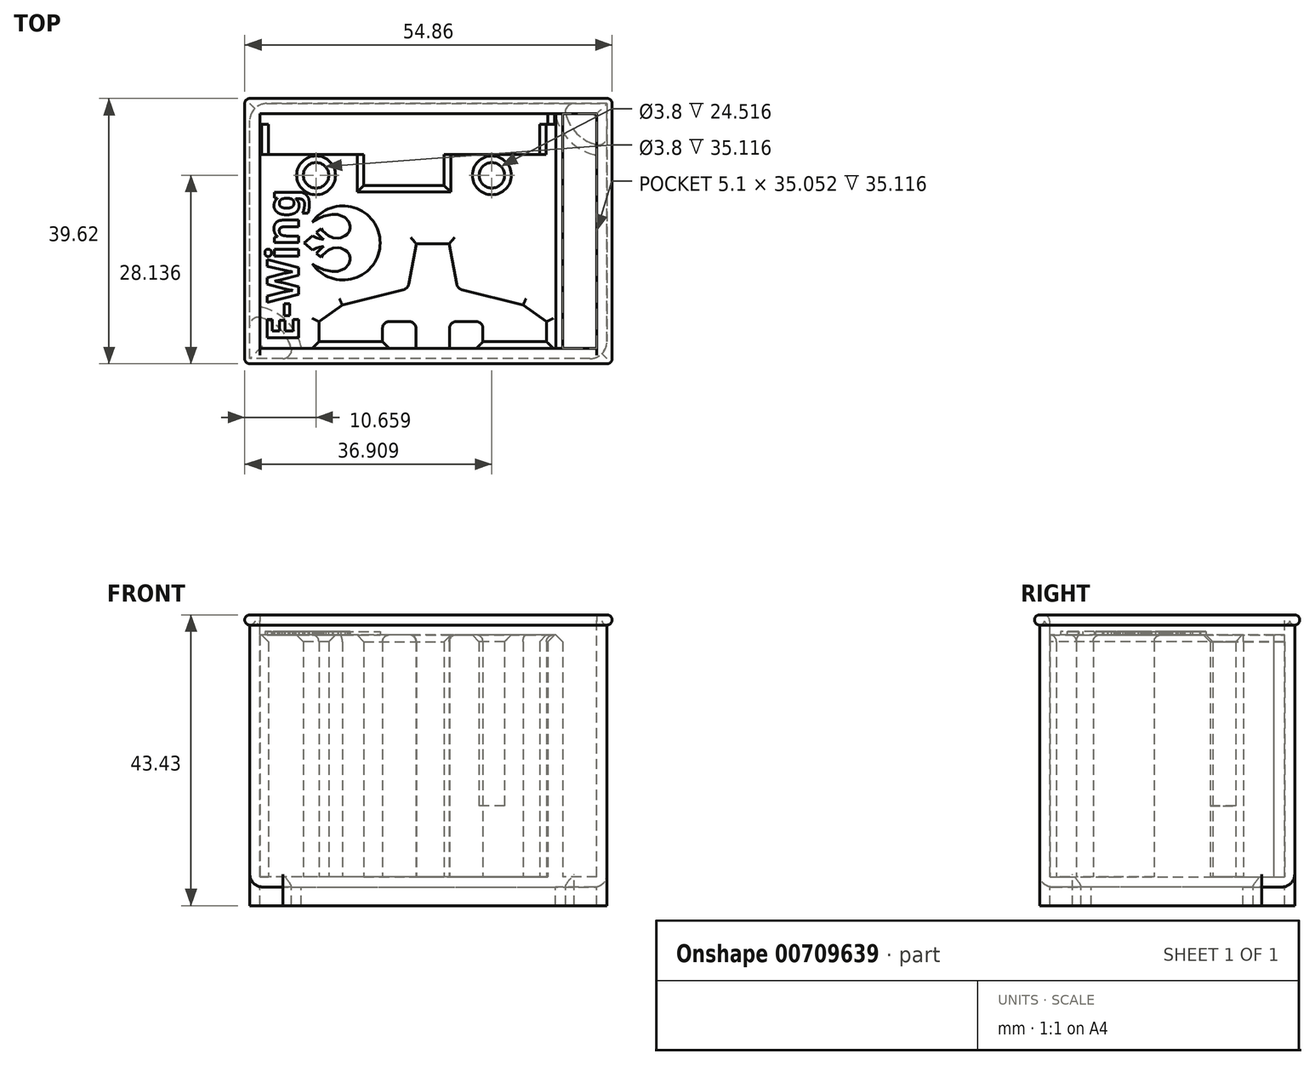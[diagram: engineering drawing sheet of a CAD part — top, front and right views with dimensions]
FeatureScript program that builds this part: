
annotation { "Feature Type Name" : "Feature", "Feature Type Description" : "" }
export const myFeature = defineFeature(function(context is Context, id is Id, definition is map)
    precondition{}
    {
        {
            var Q0;
            Q0=qCreatedBy(makeId("Front.planeOp"),FACE);
            var sketch = newSketch(context, id + "F0", { "sketchPlane" : qUnion([Q0])});
            skLineSegment(sketch, "E0.bottom", {"start": v(26.67, -20.32) * mm, "end": v(-26.67, -20.32) * mm});
            skLineSegment(sketch, "E0.top", {"start": v(26.67, 20.32) * mm, "end": v(-26.67, 20.32) * mm});
            skLineSegment(sketch, "E0.left", {"start": v(26.67, -20.32) * mm, "end": v(26.67, 20.32) * mm});
            skLineSegment(sketch, "E0.right", {"start": v(-26.67, -20.32) * mm, "end": v(-26.67, 20.32) * mm});
            skPoint(sketch, "E0.middle", {"position": v(0, 0) * mm});
            skSolve(sketch);
        }
        {
            var Q0;
            Q0=makeQuery(id+"F0.imprint","IMPRINT",FACE,{"disambiguationData":[TD([[makeQuery(id+"F0.imprint","IMPRINT",EDGE,{"derivedFrom":sQuery(id+"F0.wireOp",EDGE,"E0.bottom")}),-1.0]])]});
            extrude(context, id + "F1", {"entities" : qUnion([Q0]), "depth" : 38.1 * mm, "symmetric" : true});
        }
        {
            var Q0;
            Q0=makeQuery(id+"F1.opExtrude","SWEPT_FACE",FACE,{"disambiguationData":[OSD([sQuery(id+"F0.wireOp",EDGE,"E0.top")])]});
            shell(context, id + "F2", {"entities" : qUnion([Q0]), "thickness" : 1.52 * mm});
        }
        {
            var Q0;
            Q0=makeQuery(id+"F1.opExtrude","CAP_FACE",FACE,{"disambiguationData":[OSD([sQuery(id+"F0.wireOp",EDGE,"E0.bottom"),sQuery(id+"F0.wireOp",EDGE,"E0.top"),sQuery(id+"F0.wireOp",EDGE,"E0.left"),sQuery(id+"F0.wireOp",EDGE,"E0.right")])],"isStart":false});
            var sketch = newSketch(context, id + "F3", { "sketchPlane" : qUnion([Q0])});
            skArc(sketch, "E1", {"start": v(-26.67, 20.32) * mm, "mid": v(-27.43, 19.56) * mm, "end": v(-26.67, 18.8) * mm});
            skSolve(sketch);
        }
        {
            var Q0;
            {var subQ0=sQuery(id+"F3.wireOp",EDGE,"E1");Q0=makeQuery(id+"F3.imprint","IMPRINT",FACE,{"disambiguationData":[TD([[makeQuery(id+"F3.imprint","IMPRINT",EDGE,{"derivedFrom":subQ0}),1.0]])]});}
            var Q1;
            Q1=makeQuery(id+"F1.opExtrude","SWEPT_EDGE",EDGE,{"disambiguationData":[OSD([sQuery(id+"F0.wireOp",EDGE,"E0.top"),sQuery(id+"F0.wireOp",EDGE,"E0.right")])]});
            var Q2;
            Q2=makeQuery(id+"F1.opExtrude","CAP_EDGE",EDGE,{"disambiguationData":[OSD([sQuery(id+"F0.wireOp",EDGE,"E0.top")])],"isStart":true});
            var Q3;
            Q3=makeQuery(id+"F1.opExtrude","SWEPT_EDGE",EDGE,{"disambiguationData":[OSD([sQuery(id+"F0.wireOp",EDGE,"E0.top"),sQuery(id+"F0.wireOp",EDGE,"E0.left")])]});
            var Q4;
            Q4=makeQuery(id+"F1.opExtrude","CAP_EDGE",EDGE,{"disambiguationData":[OSD([sQuery(id+"F0.wireOp",EDGE,"E0.top")])],"isStart":false});
            sweep(context, id + "F4", {"operationType" : NewBodyOperationType.ADD, "profiles" : qUnion([Q0]), "path" : qUnion([Q1, Q2, Q3, Q4])});
        }
        {
            var Q0;
            Q0=makeQuery(id+"F1.opExtrude","SWEPT_FACE",FACE,{"disambiguationData":[OSD([sQuery(id+"F0.wireOp",EDGE,"E0.bottom")])]});
            var sketch = newSketch(context, id + "F5", { "sketchPlane" : qUnion([Q0])});
            skLineSegment(sketch, "E2.bottom", {"start": v(26.67, 19.05) * mm, "end": v(21.75, 19.05) * mm});
            skLineSegment(sketch, "E2.left", {"start": v(26.67, 19.05) * mm, "end": v(26.67, 14.13) * mm});
            skPoint(sketch, "E3.newPointA", {"position": v(20.32, 19.05) * mm});
            skArc(sketch, "E4", {"start": v(20.52, 17.46) * mm, "mid": v(22.18, 14.56) * mm, "end": v(25.08, 12.9) * mm});
            skArc(sketch, "E5.filletArc", {"start": v(21.75, 19.05) * mm, "mid": v(20.75, 18.56) * mm, "end": v(20.52, 17.46) * mm});
            skPoint(sketch, "E6.visualSharp", {"position": v(26.67, 12.7) * mm});
            skArc(sketch, "E6.filletArc", {"start": v(25.08, 12.9) * mm, "mid": v(26.18, 13.13) * mm, "end": v(26.67, 14.13) * mm});
            skArc(sketch, "E7.MirrorCS", {"start": v(-21.75, 19.05) * mm, "mid": v(-20.75, 18.56) * mm, "end": v(-20.52, 17.46) * mm});
            skArc(sketch, "E8.MirrorCS", {"start": v(-20.52, 17.46) * mm, "mid": v(-22.18, 14.56) * mm, "end": v(-25.08, 12.9) * mm});
            skArc(sketch, "E9.MirrorCS", {"start": v(-25.08, 12.9) * mm, "mid": v(-26.18, 13.13) * mm, "end": v(-26.67, 14.13) * mm});
            skLineSegment(sketch, "E10.MirrorCS", {"start": v(-26.67, 19.05) * mm, "end": v(-26.67, 14.13) * mm});
            skLineSegment(sketch, "E11.MirrorCS", {"start": v(-26.67, 19.05) * mm, "end": v(-21.75, 19.05) * mm});
            skArc(sketch, "E12.MirrorCS", {"start": v(-20.52, -17.46) * mm, "mid": v(-22.18, -14.56) * mm, "end": v(-25.08, -12.9) * mm});
            skArc(sketch, "E13.MirrorCS", {"start": v(-21.75, -19.05) * mm, "mid": v(-20.75, -18.56) * mm, "end": v(-20.52, -17.46) * mm});
            skLineSegment(sketch, "E14.MirrorCS", {"start": v(-26.67, -19.05) * mm, "end": v(-21.75, -19.05) * mm});
            skLineSegment(sketch, "E15.MirrorCS", {"start": v(-26.67, -19.05) * mm, "end": v(-26.67, -14.13) * mm});
            skArc(sketch, "E16.MirrorCS", {"start": v(-25.08, -12.9) * mm, "mid": v(-26.18, -13.13) * mm, "end": v(-26.67, -14.13) * mm});
            skArc(sketch, "E17.MirrorCS", {"start": v(21.75, -19.05) * mm, "mid": v(20.75, -18.56) * mm, "end": v(20.52, -17.46) * mm});
            skArc(sketch, "E18.MirrorCS", {"start": v(20.52, -17.46) * mm, "mid": v(22.18, -14.56) * mm, "end": v(25.08, -12.9) * mm});
            skArc(sketch, "E19.MirrorCS", {"start": v(25.08, -12.9) * mm, "mid": v(26.18, -13.13) * mm, "end": v(26.67, -14.13) * mm});
            skLineSegment(sketch, "E20.MirrorCS", {"start": v(26.67, -19.05) * mm, "end": v(26.67, -14.13) * mm});
            skLineSegment(sketch, "E21.MirrorCS", {"start": v(26.67, -19.05) * mm, "end": v(21.75, -19.05) * mm});
            skSolve(sketch);
        }
        {
            var Q0;
            Q0=makeQuery(id+"F5.imprint","IMPRINT",FACE,{"disambiguationData":[TD([[makeQuery(id+"F5.imprint","IMPRINT",EDGE,{"derivedFrom":sQuery(id+"F5.wireOp",EDGE,"E2.bottom")}),1.0]])]});
            var Q1;
            Q1=makeQuery(id+"F5.imprint","IMPRINT",FACE,{"disambiguationData":[TD([[makeQuery(id+"F5.imprint","IMPRINT",EDGE,{"derivedFrom":sQuery(id+"F5.wireOp",EDGE,"E8.MirrorCS")}),-1.0]])]});
            var Q2;
            Q2=makeQuery(id+"F5.imprint","IMPRINT",FACE,{"disambiguationData":[TD([[makeQuery(id+"F5.imprint","IMPRINT",EDGE,{"derivedFrom":sQuery(id+"F5.wireOp",EDGE,"E12.MirrorCS")}),1.0]])]});
            var Q3;
            Q3=makeQuery(id+"F5.imprint","IMPRINT",FACE,{"disambiguationData":[TD([[makeQuery(id+"F5.imprint","IMPRINT",EDGE,{"derivedFrom":sQuery(id+"F5.wireOp",EDGE,"E17.MirrorCS")}),-1.0]])]});
            extrude(context, id + "F6", {"entities" : qUnion([Q0, Q1, Q2, Q3]), "operationType" : NewBodyOperationType.ADD, "depth" : 2.8 * mm});
        }
        {
            var Q0;
            Q0=makeQuery(id+"F6.opExtrude","CAP_FACE",FACE,{"disambiguationData":[OSD([sQuery(id+"F5.wireOp",EDGE,"E2.bottom"),sQuery(id+"F5.wireOp",EDGE,"E2.left"),sQuery(id+"F5.wireOp",EDGE,"E4"),sQuery(id+"F5.wireOp",EDGE,"E5.filletArc"),sQuery(id+"F5.wireOp",EDGE,"E6.filletArc")])],"isStart":false});
            var Q1;
            Q1=makeQuery(id+"F6.opExtrude","CAP_FACE",FACE,{"disambiguationData":[OSD([sQuery(id+"F5.wireOp",EDGE,"E8.MirrorCS"),sQuery(id+"F5.wireOp",EDGE,"E9.MirrorCS"),sQuery(id+"F5.wireOp",EDGE,"E10.MirrorCS"),sQuery(id+"F5.wireOp",EDGE,"E7.MirrorCS"),sQuery(id+"F5.wireOp",EDGE,"E11.MirrorCS")])],"isStart":false});
            var Q2;
            Q2=makeQuery(id+"F6.opExtrude","CAP_FACE",FACE,{"disambiguationData":[OSD([sQuery(id+"F5.wireOp",EDGE,"E12.MirrorCS"),sQuery(id+"F5.wireOp",EDGE,"E13.MirrorCS"),sQuery(id+"F5.wireOp",EDGE,"E14.MirrorCS"),sQuery(id+"F5.wireOp",EDGE,"E15.MirrorCS"),sQuery(id+"F5.wireOp",EDGE,"E16.MirrorCS")])],"isStart":false});
            var Q3;
            Q3=makeQuery(id+"F6.opExtrude","CAP_FACE",FACE,{"disambiguationData":[OSD([sQuery(id+"F5.wireOp",EDGE,"E17.MirrorCS"),sQuery(id+"F5.wireOp",EDGE,"E18.MirrorCS"),sQuery(id+"F5.wireOp",EDGE,"E19.MirrorCS"),sQuery(id+"F5.wireOp",EDGE,"E20.MirrorCS"),sQuery(id+"F5.wireOp",EDGE,"E21.MirrorCS")])],"isStart":false});
            shell(context, id + "F7", {"entities" : qUnion([Q0, Q1, Q2, Q3]), "thickness" : 1.52 * mm});
        }
        {
            var Q0;
            Q0=makeQuery(id+"F1.opExtrude","SWEPT_EDGE",EDGE,{"disambiguationData":[OSD([sQuery(id+"F0.wireOp",EDGE,"E0.bottom"),sQuery(id+"F0.wireOp",EDGE,"E0.right")])]});
            var Q1;
            Q1=makeQuery(id+"F1.opExtrude","CAP_EDGE",EDGE,{"disambiguationData":[OSD([sQuery(id+"F0.wireOp",EDGE,"E0.bottom")])],"isStart":false});
            var Q2;
            Q2=makeQuery(id+"F1.opExtrude","SWEPT_EDGE",EDGE,{"disambiguationData":[OSD([sQuery(id+"F0.wireOp",EDGE,"E0.bottom"),sQuery(id+"F0.wireOp",EDGE,"E0.left")])]});
            var Q3;
            Q3=makeQuery(id+"F1.opExtrude","CAP_EDGE",EDGE,{"disambiguationData":[OSD([sQuery(id+"F0.wireOp",EDGE,"E0.bottom")])],"isStart":true});
            fillet(context, id + "F8", {"entities" : qUnion([Q0, Q1, Q2, Q3]), "radius" : 1.9 * mm, "tangentPropagation" : true, "allowEdgeOverflow" : false});
        }
        {
            var Q0;
            Q0=makeQuery(id+"F4.opSweep","MID_CAP_EDGE",EDGE,{"disambiguationData":[OSD([sQuery(id+"F0.wireOp",EDGE,"E0.top"),sQuery(id+"F0.wireOp",EDGE,"E0.left"),sQuery(id+"F3.wireOp",EDGE,"E1")])],"capPos":3.0});
            var Q1;
            Q1=makeQuery(id+"F4.opSweep","MID_CAP_EDGE",EDGE,{"disambiguationData":[OSD([sQuery(id+"F0.wireOp",EDGE,"E0.top"),sQuery(id+"F0.wireOp",EDGE,"E0.left"),sQuery(id+"F3.wireOp",EDGE,"E1")])],"capPos":2.0});
            var Q2;
            Q2=makeQuery(id+"F4.opSweep","MID_CAP_EDGE",EDGE,{"disambiguationData":[OSD([sQuery(id+"F0.wireOp",EDGE,"E0.top"),sQuery(id+"F0.wireOp",EDGE,"E0.right"),sQuery(id+"F3.wireOp",EDGE,"E1")])],"capPos":1.0});
            var Q3;
            Q3=makeQuery(id+"F4.opSweep","CAP_EDGE",EDGE,{"disambiguationData":[OSD([sQuery(id+"F0.wireOp",EDGE,"E0.top"),sQuery(id+"F0.wireOp",EDGE,"E0.right"),sQuery(id+"F3.wireOp",EDGE,"E1")])],"isStart":true});
            fillet(context, id + "F9", {"entities" : qUnion([Q0, Q1, Q2, Q3]), "radius" : 0.76 * mm, "tangentPropagation" : true, "allowEdgeOverflow" : false});
        }
        {
            var Q0;
            Q0=makeQuery(id+"F6.boolean.opBoolean","MERGE",EDGE,{"derivedFrom":[makeQuery(id+"F1.opExtrude","CAP_EDGE",EDGE,{"disambiguationData":[OSD([sQuery(id+"F0.wireOp",EDGE,"E0.left")])],"isStart":false}),makeQuery(id+"F6.opExtrude","SWEPT_EDGE",EDGE,{"disambiguationData":[OSD([sQuery(id+"F5.wireOp",EDGE,"E2.bottom"),sQuery(id+"F5.wireOp",EDGE,"E2.left")])]})]});
            var Q1;
            Q1=makeQuery(id+"F6.boolean.opBoolean","MERGE",EDGE,{"derivedFrom":[makeQuery(id+"F1.opExtrude","CAP_EDGE",EDGE,{"disambiguationData":[OSD([sQuery(id+"F0.wireOp",EDGE,"E0.left")])],"isStart":true}),makeQuery(id+"F6.opExtrude","SWEPT_EDGE",EDGE,{"disambiguationData":[OSD([sQuery(id+"F5.wireOp",EDGE,"E20.MirrorCS"),sQuery(id+"F5.wireOp",EDGE,"E21.MirrorCS")])]})]});
            var Q2;
            Q2=makeQuery(id+"F6.boolean.opBoolean","MERGE",EDGE,{"derivedFrom":[makeQuery(id+"F1.opExtrude","CAP_EDGE",EDGE,{"disambiguationData":[OSD([sQuery(id+"F0.wireOp",EDGE,"E0.right")])],"isStart":false}),makeQuery(id+"F6.opExtrude","SWEPT_EDGE",EDGE,{"disambiguationData":[OSD([sQuery(id+"F5.wireOp",EDGE,"E10.MirrorCS"),sQuery(id+"F5.wireOp",EDGE,"E11.MirrorCS")])]})]});
            var Q3;
            Q3=makeQuery(id+"F6.boolean.opBoolean","MERGE",EDGE,{"derivedFrom":[makeQuery(id+"F1.opExtrude","CAP_EDGE",EDGE,{"disambiguationData":[OSD([sQuery(id+"F0.wireOp",EDGE,"E0.right")])],"isStart":true}),makeQuery(id+"F6.opExtrude","SWEPT_EDGE",EDGE,{"disambiguationData":[OSD([sQuery(id+"F5.wireOp",EDGE,"E14.MirrorCS"),sQuery(id+"F5.wireOp",EDGE,"E15.MirrorCS")])]})]});
            fillet(context, id + "F10", {"entities" : qUnion([Q0, Q1, Q2, Q3]), "radius" : 2.54 * mm, "tangentPropagation" : true, "allowEdgeOverflow" : false});
        }
        {
            var Q0;
            Q0=makeQuery(id+"F2.opShell","OFFSET_FACE",FACE,{"disambiguationData":[OSD([sQuery(id+"F0.wireOp",EDGE,"E0.bottom")])]});
            var sketch = newSketch(context, id + "F11", { "sketchPlane" : qUnion([Q0])});
            skLineSegment(sketch, "E22.bottom", {"start": v(-51.93, -9.02) * mm, "end": v(-66.18, -9.02) * mm});
            skLineSegment(sketch, "E22.top", {"start": v(-51.93, -2.92) * mm, "end": v(-92.43, -2.92) * mm});
            skLineSegment(sketch, "E22.left", {"start": v(-51.93, -9.02) * mm, "end": v(-51.93, -4.52) * mm});
            skLineSegment(sketch, "E22.right", {"start": v(-92.43, -9.02) * mm, "end": v(-92.43, -4.52) * mm});
            skPoint(sketch, "E22.middle", {"position": v(-72.18, -5.97) * mm});
            skLineSegment(sketch, "E23.bottom", {"start": v(-93.68, -2.92) * mm, "end": v(-50.68, -2.92) * mm});
            skLineSegment(sketch, "E23.top", {"start": v(-93.68, -4.52) * mm, "end": v(-92.43, -4.52) * mm});
            skLineSegment(sketch, "E23.left", {"start": v(-93.68, -2.92) * mm, "end": v(-93.68, -4.52) * mm});
            skLineSegment(sketch, "E23.right", {"start": v(-50.68, -2.92) * mm, "end": v(-50.68, -4.52) * mm});
            skLineSegment(sketch, "E24.top", {"start": v(-78.18, -13.62) * mm, "end": v(-66.18, -13.62) * mm});
            skLineSegment(sketch, "E24.left", {"start": v(-78.18, -9.02) * mm, "end": v(-78.18, -13.62) * mm});
            skLineSegment(sketch, "E24.right", {"start": v(-66.18, -9.02) * mm, "end": v(-66.18, -13.62) * mm});
            skLineSegment(sketch, "E25.trimOffspring", {"start": v(-51.93, -4.52) * mm, "end": v(-50.68, -4.52) * mm});
            skLineSegment(sketch, "E26.trimOffspring", {"start": v(-78.18, -9.02) * mm, "end": v(-92.43, -9.02) * mm});
            skCircle(sketch, "E27", {"center": v(-59.06, -12.12) * mm, "radius": 1.9 * mm});
            skLineSegment(sketch, "E28", {"start": v(-59.06, -9.02) * mm, "end": v(-59.06, -10.22) * mm, "construction": true});
            skPoint(sketch, "E29.startSnap0", {"position": v(-72.18, -2.92) * mm});
            skLineSegment(sketch, "E30.MirrorCS", {"start": v(-85.3, -9.02) * mm, "end": v(-85.3, -10.22) * mm, "construction": true});
            skCircle(sketch, "E31.MirrorC", {"center": v(-85.3, -12.12) * mm, "radius": 1.9 * mm});
            skLineSegment(sketch, "E32.bottom", {"start": v(16.6, 11.43) * mm, "end": v(2.35, 11.43) * mm});
            skLineSegment(sketch, "E32.top", {"start": v(16.6, 17.53) * mm, "end": v(-23.9, 17.53) * mm});
            skLineSegment(sketch, "E32.left", {"start": v(16.6, 11.43) * mm, "end": v(16.6, 15.93) * mm});
            skLineSegment(sketch, "E32.right", {"start": v(-23.9, 11.43) * mm, "end": v(-23.9, 15.93) * mm});
            skPoint(sketch, "E32.middle", {"position": v(-3.65, 14.48) * mm});
            skLineSegment(sketch, "E33.bottom", {"start": v(-25.15, 17.53) * mm, "end": v(17.85, 17.53) * mm});
            skLineSegment(sketch, "E33.top", {"start": v(-25.15, 15.93) * mm, "end": v(-23.9, 15.93) * mm});
            skLineSegment(sketch, "E33.left", {"start": v(-25.15, 17.53) * mm, "end": v(-25.15, 15.93) * mm});
            skLineSegment(sketch, "E33.right", {"start": v(17.85, 17.53) * mm, "end": v(17.85, 15.93) * mm});
            skLineSegment(sketch, "E34.top", {"start": v(-9.65, 6.83) * mm, "end": v(2.35, 6.83) * mm});
            skLineSegment(sketch, "E34.left", {"start": v(-9.65, 11.43) * mm, "end": v(-9.65, 6.83) * mm});
            skLineSegment(sketch, "E34.right", {"start": v(2.35, 11.43) * mm, "end": v(2.35, 6.83) * mm});
            skLineSegment(sketch, "E35.trimOffspring", {"start": v(16.6, 15.93) * mm, "end": v(17.85, 15.93) * mm});
            skLineSegment(sketch, "E36.trimOffspring", {"start": v(-9.65, 11.43) * mm, "end": v(-23.9, 11.43) * mm});
            skCircle(sketch, "E37", {"center": v(9.48, 8.33) * mm, "radius": 1.9 * mm});
            skLineSegment(sketch, "E38", {"start": v(9.48, 11.43) * mm, "end": v(9.48, 10.23) * mm, "construction": true});
            skPoint(sketch, "E39.startSnap0", {"position": v(-3.65, 17.53) * mm});
            skLineSegment(sketch, "E40.MirrorCS", {"start": v(-16.77, 11.43) * mm, "end": v(-16.77, 10.23) * mm, "construction": true});
            skCircle(sketch, "E41.MirrorC", {"center": v(-16.77, 8.33) * mm, "radius": 1.9 * mm});
            skSolve(sketch);
        }
        {
            var Q0;
            Q0=makeQuery(id+"F2.opShell","OFFSET_FACE",FACE,{"disambiguationData":[OSD([sQuery(id+"F0.wireOp",EDGE,"E0.bottom")])]});
            var sketch = newSketch(context, id + "F12", { "sketchPlane" : qUnion([Q0])});
            skLineSegment(sketch, "E42.bottom", {"start": v(20.05, -17.7) * mm, "end": v(20.05, 17.7) * mm});
            skLineSegment(sketch, "E42.top", {"start": v(25.15, -17.7) * mm, "end": v(25.15, 17.7) * mm});
            skLineSegment(sketch, "E42.left", {"start": v(20.05, -17.7) * mm, "end": v(25.15, -17.7) * mm});
            skLineSegment(sketch, "E42.right", {"start": v(20.05, 17.7) * mm, "end": v(25.15, 17.7) * mm});
            skPoint(sketch, "E42.middle", {"position": v(22.6, 0) * mm});
            skSolve(sketch);
        }
        {
            var Q0;
            Q0=makeQuery(id+"F2.opShell","OFFSET_FACE",FACE,{"disambiguationData":[OSD([sQuery(id+"F0.wireOp",EDGE,"E0.bottom")])]});
            var sketch = newSketch(context, id + "F13", { "sketchPlane" : qUnion([Q0])});
            skLineSegment(sketch, "E43", {"start": v(-1.2, -17.53) * mm, "end": v(-3.65, -17.53) * mm});
            skLineSegment(sketch, "E44.MirrorCS", {"start": v(-6.1, -17.53) * mm, "end": v(-3.65, -17.53) * mm});
            skLineSegment(sketch, "E45", {"start": v(-1.15, -17.53) * mm, "end": v(-1.15, -13.53) * mm});
            skLineSegment(sketch, "E46", {"start": v(-1.15, -13.53) * mm, "end": v(3.85, -13.53) * mm});
            skLineSegment(sketch, "E47", {"start": v(3.85, -13.53) * mm, "end": v(3.85, -16.53) * mm});
            skPoint(sketch, "E48.visualSharp", {"position": v(3.85, -13.53) * mm});
            skPoint(sketch, "E49.visualSharp", {"position": v(-1.15, -13.53) * mm});
            skLineSegment(sketch, "E50", {"start": v(-1.15, -17.53) * mm, "end": v(-3.65, -17.53) * mm});
            skLineSegment(sketch, "E51", {"start": v(-1.2, -1.93) * mm, "end": v(-3.65, -1.93) * mm});
            skLineSegment(sketch, "E52", {"start": v(13.35, -16.53) * mm, "end": v(13.35, -13.53) * mm});
            skLineSegment(sketch, "E53", {"start": v(0.05, -8.58) * mm, "end": v(9.85, -11.03) * mm});
            skLineSegment(sketch, "E54", {"start": v(9.85, -11.03) * mm, "end": v(13.35, -13.53) * mm});
            skLineSegment(sketch, "E55", {"start": v(3.85, -16.53) * mm, "end": v(13.35, -16.53) * mm});
            skLineSegment(sketch, "E56", {"start": v(-1.2, -1.93) * mm, "end": v(0.05, -8.58) * mm});
            skLineSegment(sketch, "E57.MirrorCS", {"start": v(-6.1, -1.93) * mm, "end": v(-3.65, -1.93) * mm});
            skLineSegment(sketch, "E58.MirrorCS", {"start": v(-11.15, -13.53) * mm, "end": v(-11.15, -16.53) * mm});
            skLineSegment(sketch, "E59.MirrorCS", {"start": v(-6.15, -13.53) * mm, "end": v(-11.15, -13.53) * mm});
            skLineSegment(sketch, "E60.MirrorCS", {"start": v(-6.15, -17.53) * mm, "end": v(-3.65, -17.53) * mm});
            skLineSegment(sketch, "E61.MirrorCS", {"start": v(-11.15, -16.53) * mm, "end": v(-20.65, -16.53) * mm});
            skLineSegment(sketch, "E62.MirrorCS", {"start": v(-6.15, -17.53) * mm, "end": v(-6.15, -13.53) * mm});
            skPoint(sketch, "E63.MirrorP", {"position": v(-6.15, -13.53) * mm});
            skPoint(sketch, "E64.MirrorP", {"position": v(-11.15, -13.53) * mm});
            skLineSegment(sketch, "E65.MirrorCS", {"start": v(-20.65, -16.53) * mm, "end": v(-20.65, -13.53) * mm});
            skLineSegment(sketch, "E66.MirrorCS", {"start": v(-7.34, -8.58) * mm, "end": v(-17.15, -11.03) * mm});
            skLineSegment(sketch, "E67.MirrorCS", {"start": v(-6.1, -1.93) * mm, "end": v(-7.34, -8.58) * mm});
            skLineSegment(sketch, "E68.MirrorCS", {"start": v(-17.15, -11.03) * mm, "end": v(-20.65, -13.53) * mm});
            skPoint(sketch, "E69.0", {"position": v(-3.65, 6.83) * mm});
            skSolve(sketch);
        }
        {
            var Q0;
            Q0=makeQuery(id+"F2.opShell","OFFSET_FACE",FACE,{"disambiguationData":[OSD([sQuery(id+"F0.wireOp",EDGE,"E0.bottom")])]});
            var sketch = newSketch(context, id + "F14", { "sketchPlane" : qUnion([Q0])});
            skLineSegment(sketch, "E70.0", {"start": v(3.1, -17.53) * mm, "end": v(0.65, -17.53) * mm});
            skLineSegment(sketch, "E70.1", {"start": v(-1.8, -17.53) * mm, "end": v(0.65, -17.53) * mm});
            skLineSegment(sketch, "E70.2", {"start": v(3.15, -17.53) * mm, "end": v(3.15, -13.53) * mm});
            skLineSegment(sketch, "E70.3", {"start": v(3.15, -13.53) * mm, "end": v(8.15, -13.53) * mm});
            skLineSegment(sketch, "E70.4", {"start": v(8.15, -13.53) * mm, "end": v(8.15, -16.53) * mm});
            skPoint(sketch, "E70.5", {"position": v(8.15, -13.53) * mm});
            skPoint(sketch, "E70.6", {"position": v(3.15, -13.53) * mm});
            skLineSegment(sketch, "E70.7", {"start": v(3.15, -17.53) * mm, "end": v(0.65, -17.53) * mm});
            skLineSegment(sketch, "E70.8", {"start": v(3.1, -1.93) * mm, "end": v(0.65, -1.93) * mm});
            skLineSegment(sketch, "E70.9", {"start": v(17.65, -16.53) * mm, "end": v(17.65, -13.53) * mm});
            skLineSegment(sketch, "E70.10", {"start": v(4.34, -8.58) * mm, "end": v(14.15, -11.03) * mm});
            skLineSegment(sketch, "E70.11", {"start": v(14.15, -11.03) * mm, "end": v(17.65, -13.53) * mm});
            skLineSegment(sketch, "E70.12", {"start": v(8.15, -16.53) * mm, "end": v(17.65, -16.53) * mm});
            skLineSegment(sketch, "E70.13", {"start": v(3.1, -1.93) * mm, "end": v(4.34, -8.58) * mm});
            skLineSegment(sketch, "E70.14", {"start": v(-1.8, -1.93) * mm, "end": v(0.65, -1.93) * mm});
            skLineSegment(sketch, "E70.15", {"start": v(-6.85, -13.53) * mm, "end": v(-6.85, -16.53) * mm});
            skLineSegment(sketch, "E70.16", {"start": v(-1.85, -13.53) * mm, "end": v(-6.85, -13.53) * mm});
            skLineSegment(sketch, "E70.17", {"start": v(-1.85, -17.53) * mm, "end": v(0.65, -17.53) * mm});
            skLineSegment(sketch, "E70.18", {"start": v(-6.85, -16.53) * mm, "end": v(-16.35, -16.53) * mm});
            skLineSegment(sketch, "E70.19", {"start": v(-1.85, -17.53) * mm, "end": v(-1.85, -13.53) * mm});
            skPoint(sketch, "E70.20", {"position": v(-1.85, -13.53) * mm});
            skPoint(sketch, "E70.21", {"position": v(-6.85, -13.53) * mm});
            skLineSegment(sketch, "E70.22", {"start": v(-16.35, -16.53) * mm, "end": v(-16.35, -13.53) * mm});
            skLineSegment(sketch, "E70.23", {"start": v(-3.05, -8.58) * mm, "end": v(-12.85, -11.03) * mm});
            skLineSegment(sketch, "E70.24", {"start": v(-1.8, -1.93) * mm, "end": v(-3.05, -8.58) * mm});
            skLineSegment(sketch, "E70.25", {"start": v(-12.85, -11.03) * mm, "end": v(-16.35, -13.53) * mm});
            skPoint(sketch, "E70.26", {"position": v(-3.65, 6.83) * mm});
            skLineSegment(sketch, "E71.0", {"start": v(20.05, -17.7) * mm, "end": v(20.05, 17.7) * mm});
            skLineSegment(sketch, "E71.1", {"start": v(25.15, -17.7) * mm, "end": v(25.15, 17.7) * mm});
            skLineSegment(sketch, "E71.2", {"start": v(20.05, -17.7) * mm, "end": v(25.15, -17.7) * mm});
            skLineSegment(sketch, "E71.3", {"start": v(20.05, 17.7) * mm, "end": v(25.15, 17.7) * mm});
            skPoint(sketch, "E71.4", {"position": v(22.6, 0) * mm});
            skLineSegment(sketch, "E71.5", {"start": v(-51.93, -9.02) * mm, "end": v(-66.18, -9.02) * mm});
            skLineSegment(sketch, "E71.6", {"start": v(-51.93, -2.92) * mm, "end": v(-92.43, -2.92) * mm});
            skLineSegment(sketch, "E71.7", {"start": v(-51.93, -9.02) * mm, "end": v(-51.93, -4.52) * mm});
            skLineSegment(sketch, "E71.8", {"start": v(-92.43, -9.02) * mm, "end": v(-92.43, -4.52) * mm});
            skPoint(sketch, "E71.9", {"position": v(-72.18, -5.97) * mm});
            skLineSegment(sketch, "E71.10", {"start": v(-93.68, -2.92) * mm, "end": v(-50.68, -2.92) * mm});
            skLineSegment(sketch, "E71.11", {"start": v(-93.68, -4.52) * mm, "end": v(-92.43, -4.52) * mm});
            skLineSegment(sketch, "E71.12", {"start": v(-93.68, -2.92) * mm, "end": v(-93.68, -4.52) * mm});
            skLineSegment(sketch, "E71.13", {"start": v(-50.68, -2.92) * mm, "end": v(-50.68, -4.52) * mm});
            skLineSegment(sketch, "E71.14", {"start": v(-78.18, -13.62) * mm, "end": v(-66.18, -13.62) * mm});
            skLineSegment(sketch, "E71.15", {"start": v(-78.18, -9.02) * mm, "end": v(-78.18, -13.62) * mm});
            skLineSegment(sketch, "E71.16", {"start": v(-66.18, -9.02) * mm, "end": v(-66.18, -13.62) * mm});
            skLineSegment(sketch, "E71.17", {"start": v(-51.93, -4.52) * mm, "end": v(-50.68, -4.52) * mm});
            skLineSegment(sketch, "E71.18", {"start": v(-78.18, -9.02) * mm, "end": v(-92.43, -9.02) * mm});
            skCircle(sketch, "E71.19", {"center": v(-59.06, -12.12) * mm, "radius": 1.9 * mm});
            skLineSegment(sketch, "E71.20", {"start": v(-59.06, -9.02) * mm, "end": v(-59.06, -10.22) * mm});
            skPoint(sketch, "E71.21", {"position": v(-72.18, -2.92) * mm});
            skLineSegment(sketch, "E71.22", {"start": v(-85.3, -9.02) * mm, "end": v(-85.3, -10.22) * mm});
            skCircle(sketch, "E71.23", {"center": v(-85.3, -12.12) * mm, "radius": 1.9 * mm});
            skLineSegment(sketch, "E71.24", {"start": v(16.6, 11.43) * mm, "end": v(2.35, 11.43) * mm});
            skLineSegment(sketch, "E71.25", {"start": v(16.6, 17.53) * mm, "end": v(-23.9, 17.53) * mm});
            skLineSegment(sketch, "E71.26", {"start": v(16.6, 11.43) * mm, "end": v(16.6, 15.93) * mm});
            skLineSegment(sketch, "E71.27", {"start": v(-23.9, 11.43) * mm, "end": v(-23.9, 15.93) * mm});
            skPoint(sketch, "E71.28", {"position": v(-3.65, 14.48) * mm});
            skLineSegment(sketch, "E71.29", {"start": v(-25.15, 17.53) * mm, "end": v(17.85, 17.53) * mm});
            skLineSegment(sketch, "E71.30", {"start": v(-25.15, 15.93) * mm, "end": v(-23.9, 15.93) * mm});
            skLineSegment(sketch, "E71.31", {"start": v(-25.15, 17.53) * mm, "end": v(-25.15, 15.93) * mm});
            skLineSegment(sketch, "E71.32", {"start": v(17.85, 17.53) * mm, "end": v(17.85, 15.93) * mm});
            skLineSegment(sketch, "E71.33", {"start": v(-9.65, 6.83) * mm, "end": v(2.35, 6.83) * mm});
            skLineSegment(sketch, "E71.34", {"start": v(-9.65, 11.43) * mm, "end": v(-9.65, 6.83) * mm});
            skLineSegment(sketch, "E71.35", {"start": v(2.35, 11.43) * mm, "end": v(2.35, 6.83) * mm});
            skLineSegment(sketch, "E71.36", {"start": v(16.6, 15.93) * mm, "end": v(17.85, 15.93) * mm});
            skLineSegment(sketch, "E71.37", {"start": v(-9.65, 11.43) * mm, "end": v(-23.9, 11.43) * mm});
            skCircle(sketch, "E71.38", {"center": v(9.48, 8.33) * mm, "radius": 1.9 * mm});
            skLineSegment(sketch, "E71.39", {"start": v(9.48, 11.43) * mm, "end": v(9.48, 10.23) * mm});
            skPoint(sketch, "E71.40", {"position": v(-3.65, 17.53) * mm});
            skLineSegment(sketch, "E71.41", {"start": v(-16.77, 11.43) * mm, "end": v(-16.77, 10.23) * mm});
            skCircle(sketch, "E71.42", {"center": v(-16.77, 8.33) * mm, "radius": 1.9 * mm});
            skLineSegment(sketch, "E72", {"start": v(17.65, -16.53) * mm, "end": v(20.05, -16.53) * mm, "construction": true});
            skSolve(sketch);
        }
        {
            var Q0;
            Q0=makeQuery(id+"F14.imprint","IMPRINT",FACE,{"disambiguationData":[TD([[makeQuery(id+"F14.imprint","IMPRINT",EDGE,{"derivedFrom":sQuery(id+"F14.wireOp",EDGE,"E71.42")}),-1.0]])]});
            var Q1;
            Q1=makeQuery(id+"F14.imprint","IMPRINT",FACE,{"disambiguationData":[TD([[makeQuery(id+"F14.imprint","IMPRINT",EDGE,{"derivedFrom":sQuery(id+"F14.wireOp",EDGE,"E71.38")}),1.0]])]});
            extrude(context, id + "F15", {"entities" : qUnion([Q0, Q1]), "operationType" : NewBodyOperationType.ADD, "depth" : 10.6 * mm, "offsetDistance" : 25 * mm});
        }
        {
            var Q0;
            {var subQ19=sQuery(id+"F14.wireOp",EDGE,"E70.2");Q0=makeQuery(id+"F14.imprint","IMPRINT",FACE,{"disambiguationData":[TD([[makeQuery(id+"F14.imprint","IMPRINT",EDGE,{"derivedFrom":subQ19}),-1.0]])]});}
            extrude(context, id + "F16", {"entities" : qUnion([Q0]), "operationType" : NewBodyOperationType.ADD, "depth" : 36.12 * mm, "offsetDistance" : 25 * mm});
        }
        {
            var Q0;
            Q0=makeQuery(id+"F16.opExtrude","CAP_EDGE",EDGE,{"disambiguationData":[OSD([sQuery(id+"F14.wireOp",EDGE,"E71.38")])],"isStart":false});
            var Q1;
            Q1=makeQuery(id+"F16.opExtrude","CAP_EDGE",EDGE,{"disambiguationData":[OSD([sQuery(id+"F14.wireOp",EDGE,"E71.42")])],"isStart":false});
            chamfer(context, id + "F17", {"entities" : qUnion([Q0, Q1]), "width" : 1 * mm, "tangentPropagation" : true});
        }
        {
            var Q0;
            Q0=makeQuery(id+"F16.opExtrude","CAP_EDGE",EDGE,{"disambiguationData":[OSD([sQuery(id+"F14.wireOp",EDGE,"E71.34")])],"isStart":false});
            var Q1;
            Q1=makeQuery(id+"F16.opExtrude","CAP_EDGE",EDGE,{"disambiguationData":[OSD([sQuery(id+"F14.wireOp",EDGE,"E71.33")])],"isStart":false});
            var Q2;
            Q2=makeQuery(id+"F16.opExtrude","CAP_EDGE",EDGE,{"disambiguationData":[OSD([sQuery(id+"F14.wireOp",EDGE,"E71.35")])],"isStart":false});
            var Q3;
            Q3=makeQuery(id+"F16.opExtrude","CAP_EDGE",EDGE,{"disambiguationData":[OSD([sQuery(id+"F14.wireOp",EDGE,"E71.26")])],"isStart":false});
            var Q4;
            Q4=makeQuery(id+"F16.opExtrude","CAP_EDGE",EDGE,{"disambiguationData":[OSD([sQuery(id+"F14.wireOp",EDGE,"E71.27")])],"isStart":false});
            var Q5;
            Q5=makeQuery(id+"F16.opExtrude","CAP_EDGE",EDGE,{"disambiguationData":[OSD([sQuery(id+"F14.wireOp",EDGE,"E71.32")])],"isStart":false});
            var Q6;
            Q6=makeQuery(id+"F16.opExtrude","CAP_EDGE",EDGE,{"disambiguationData":[OSD([sQuery(id+"F14.wireOp",EDGE,"E71.0")])],"isStart":false});
            chamfer(context, id + "F18", {"entities" : qUnion([Q0, Q1, Q2, Q3, Q4, Q5, Q6]), "width" : 1 * mm, "tangentPropagation" : true});
        }
        {
            var Q0;
            Q0=makeQuery(id+"F16.opExtrude","CAP_EDGE",EDGE,{"disambiguationData":[OSD([sQuery(id+"F14.wireOp",EDGE,"E70.24")])],"isStart":false});
            var Q1;
            Q1=makeQuery(id+"F16.opExtrude","CAP_EDGE",EDGE,{"disambiguationData":[OSD([sQuery(id+"F14.wireOp",EDGE,"E70.8"),sQuery(id+"F14.wireOp",EDGE,"E70.14")])],"isStart":false});
            var Q2;
            Q2=makeQuery(id+"F16.opExtrude","CAP_EDGE",EDGE,{"disambiguationData":[OSD([sQuery(id+"F14.wireOp",EDGE,"E70.13")])],"isStart":false});
            var Q3;
            Q3=makeQuery(id+"F16.opExtrude","CAP_EDGE",EDGE,{"disambiguationData":[OSD([sQuery(id+"F14.wireOp",EDGE,"E70.11")])],"isStart":false});
            var Q4;
            Q4=makeQuery(id+"F16.opExtrude","CAP_EDGE",EDGE,{"disambiguationData":[OSD([sQuery(id+"F14.wireOp",EDGE,"E70.10")])],"isStart":false});
            var Q5;
            Q5=makeQuery(id+"F16.opExtrude","CAP_EDGE",EDGE,{"disambiguationData":[OSD([sQuery(id+"F14.wireOp",EDGE,"E70.9")])],"isStart":false});
            var Q6;
            Q6=makeQuery(id+"F16.opExtrude","CAP_EDGE",EDGE,{"disambiguationData":[OSD([sQuery(id+"F14.wireOp",EDGE,"E70.12")])],"isStart":false});
            var Q7;
            Q7=makeQuery(id+"F16.opExtrude","CAP_EDGE",EDGE,{"disambiguationData":[OSD([sQuery(id+"F14.wireOp",EDGE,"E70.3")])],"isStart":false});
            var Q8;
            {var subQ1=sQuery(id+"F14.wireOp",EDGE,"E70.2");var subQ5=sQuery(id+"F0.wireOp",EDGE,"E0.top");Q8=makeQuery(id+"F16.boolean.opBoolean","SPLIT",EDGE,{"disambiguationData":[TD([makeQuery(id+"F16.opExtrude","SWEPT_FACE",FACE,{"disambiguationData":[OSD([subQ1])]})])],"derivedFrom":makeQuery(id+"F2.opShell","OFFSET_EDGE",EDGE,{"disambiguationData":[OSD([subQ5]),TDD([makeQuery(id+"F1.opExtrude","CAP_EDGE",EDGE,{"disambiguationData":[OSD([subQ5])],"isStart":false})])]})});}
            var Q9;
            Q9=makeQuery(id+"F16.opExtrude","CAP_EDGE",EDGE,{"disambiguationData":[OSD([sQuery(id+"F14.wireOp",EDGE,"E70.16")])],"isStart":false});
            var Q10;
            Q10=makeQuery(id+"F16.opExtrude","CAP_EDGE",EDGE,{"disambiguationData":[OSD([sQuery(id+"F14.wireOp",EDGE,"E70.18")])],"isStart":false});
            var Q11;
            Q11=makeQuery(id+"F16.opExtrude","CAP_EDGE",EDGE,{"disambiguationData":[OSD([sQuery(id+"F14.wireOp",EDGE,"E70.2")])],"isStart":false});
            var Q12;
            Q12=makeQuery(id+"F16.opExtrude","CAP_EDGE",EDGE,{"disambiguationData":[OSD([sQuery(id+"F14.wireOp",EDGE,"E70.19")])],"isStart":false});
            var Q13;
            Q13=makeQuery(id+"F16.opExtrude","CAP_EDGE",EDGE,{"disambiguationData":[OSD([sQuery(id+"F14.wireOp",EDGE,"E70.4")])],"isStart":false});
            var Q14;
            Q14=makeQuery(id+"F16.opExtrude","CAP_EDGE",EDGE,{"disambiguationData":[OSD([sQuery(id+"F14.wireOp",EDGE,"E70.15")])],"isStart":false});
            var Q15;
            Q15=makeQuery(id+"F16.opExtrude","CAP_EDGE",EDGE,{"disambiguationData":[OSD([sQuery(id+"F14.wireOp",EDGE,"E70.23")])],"isStart":false});
            var Q16;
            Q16=makeQuery(id+"F16.opExtrude","CAP_EDGE",EDGE,{"disambiguationData":[OSD([sQuery(id+"F14.wireOp",EDGE,"E70.22")])],"isStart":false});
            var Q17;
            Q17=makeQuery(id+"F16.opExtrude","CAP_EDGE",EDGE,{"disambiguationData":[OSD([sQuery(id+"F14.wireOp",EDGE,"E70.25")])],"isStart":false});
            var Q18;
            Q18=makeQuery(id+"F16.opExtrude","SWEPT_EDGE",EDGE,{"disambiguationData":[OSD([sQuery(id+"F14.wireOp",EDGE,"E70.15"),sQuery(id+"F14.wireOp",EDGE,"E70.16")])]});
            var Q19;
            Q19=makeQuery(id+"F16.opExtrude","SWEPT_EDGE",EDGE,{"disambiguationData":[OSD([sQuery(id+"F14.wireOp",EDGE,"E70.16"),sQuery(id+"F14.wireOp",EDGE,"E70.19")])]});
            var Q20;
            Q20=makeQuery(id+"F16.opExtrude","SWEPT_EDGE",EDGE,{"disambiguationData":[OSD([sQuery(id+"F14.wireOp",EDGE,"E70.2"),sQuery(id+"F14.wireOp",EDGE,"E70.3")])]});
            var Q21;
            Q21=makeQuery(id+"F16.opExtrude","SWEPT_EDGE",EDGE,{"disambiguationData":[OSD([sQuery(id+"F14.wireOp",EDGE,"E70.3"),sQuery(id+"F14.wireOp",EDGE,"E70.4")])]});
            var Q22;
            Q22=makeQuery(id+"F16.opExtrude","SWEPT_EDGE",EDGE,{"disambiguationData":[OSD([sQuery(id+"F14.wireOp",EDGE,"E70.10"),sQuery(id+"F14.wireOp",EDGE,"E70.13")])]});
            var Q23;
            Q23=makeQuery(id+"F16.opExtrude","SWEPT_EDGE",EDGE,{"disambiguationData":[OSD([sQuery(id+"F14.wireOp",EDGE,"E70.23"),sQuery(id+"F14.wireOp",EDGE,"E70.24")])]});
            fillet(context, id + "F19", {"entities" : qUnion([Q0, Q1, Q2, Q3, Q4, Q5, Q6, Q7, Q8, Q9, Q10, Q11, Q12, Q13, Q14, Q15, Q16, Q17, Q18, Q19, Q20, Q21, Q22, Q23]), "radius" : 1 * mm, "tangentPropagation" : true, "allowEdgeOverflow" : false});
        }
        {
            var Q0;
            Q0=makeQuery(id+"F19.opFillet","SPLIT",FACE,{"disambiguationData":[OD(1.0)],"derivedFrom":makeQuery(id+"F16.opExtrude","CAP_FACE",FACE,{"disambiguationData":[OSD([sQuery(id+"F0.wireOp",EDGE,"E0.bottom"),sQuery(id+"F0.wireOp",EDGE,"E0.right"),sQuery(id+"F14.wireOp",EDGE,"E70.2"),sQuery(id+"F14.wireOp",EDGE,"E70.3"),sQuery(id+"F14.wireOp",EDGE,"E70.4"),sQuery(id+"F14.wireOp",EDGE,"E70.8"),sQuery(id+"F14.wireOp",EDGE,"E70.9"),sQuery(id+"F14.wireOp",EDGE,"E70.10"),sQuery(id+"F14.wireOp",EDGE,"E70.11"),sQuery(id+"F14.wireOp",EDGE,"E70.12"),sQuery(id+"F14.wireOp",EDGE,"E70.13"),sQuery(id+"F14.wireOp",EDGE,"E70.14"),sQuery(id+"F14.wireOp",EDGE,"E70.15"),sQuery(id+"F14.wireOp",EDGE,"E70.16"),sQuery(id+"F14.wireOp",EDGE,"E70.18"),sQuery(id+"F14.wireOp",EDGE,"E70.19"),sQuery(id+"F14.wireOp",EDGE,"E70.22"),sQuery(id+"F14.wireOp",EDGE,"E70.23"),sQuery(id+"F14.wireOp",EDGE,"E70.24"),sQuery(id+"F14.wireOp",EDGE,"E70.25"),sQuery(id+"F14.wireOp",EDGE,"E71.0"),sQuery(id+"F14.wireOp",EDGE,"E71.24"),sQuery(id+"F14.wireOp",EDGE,"E71.26"),sQuery(id+"F14.wireOp",EDGE,"E71.27"),sQuery(id+"F14.wireOp",EDGE,"E71.30"),sQuery(id+"F14.wireOp",EDGE,"E71.32"),sQuery(id+"F14.wireOp",EDGE,"E71.33"),sQuery(id+"F14.wireOp",EDGE,"E71.34"),sQuery(id+"F14.wireOp",EDGE,"E71.35"),sQuery(id+"F14.wireOp",EDGE,"E71.36"),sQuery(id+"F14.wireOp",EDGE,"E71.37"),sQuery(id+"F14.wireOp",EDGE,"E71.38"),sQuery(id+"F14.wireOp",EDGE,"E71.42")])],"isStart":false})});
            var sketch = newSketch(context, id + "F20", { "sketchPlane" : qUnion([Q0])});
            skLineSegment(sketch, "E73", {"start": v(-7.29, -37.09) * mm, "end": v(-7.29, -38.29) * mm, "construction": true});
            skLineSegment(sketch, "E74", {"start": v(-68.25, -18.83) * mm, "end": v(-68.25, -49.19) * mm, "construction": true});
            skCircle(sketch, "E75", {"center": v(-12.73, -1.77) * mm, "radius": 6.35 * mm});
            skLineSegment(sketch, "E76", {"start": v(-17.3, -0.68) * mm, "end": v(-18.54, -1.77) * mm});
            skLineSegment(sketch, "E77", {"start": v(-16.74, -0.18) * mm, "end": v(-16.03, 0.37) * mm});
            skLineSegment(sketch, "E78", {"start": v(-16.03, 0.37) * mm, "end": v(-15.8, 0.07) * mm});
            skLineSegment(sketch, "E79", {"start": v(-15.8, 0.07) * mm, "end": v(-15.34, -0.38) * mm});
            skLineSegment(sketch, "E80", {"start": v(-15.34, -0.38) * mm, "end": v(-14.94, -0.7) * mm});
            skLineSegment(sketch, "E81", {"start": v(-14.94, -0.7) * mm, "end": v(-14.24, -1) * mm});
            skLineSegment(sketch, "E82", {"start": v(-14.24, -1) * mm, "end": v(-13.49, -1.08) * mm});
            skLineSegment(sketch, "E83", {"start": v(-13.49, -1.08) * mm, "end": v(-13.12, -1) * mm});
            skLineSegment(sketch, "E84", {"start": v(-13.12, -1) * mm, "end": v(-12.43, -0.7) * mm});
            skLineSegment(sketch, "E85", {"start": v(-12.43, -0.7) * mm, "end": v(-12.11, -0.5) * mm});
            skLineSegment(sketch, "E86", {"start": v(-12.11, -0.5) * mm, "end": v(-11.82, -0.07) * mm});
            skLineSegment(sketch, "E87", {"start": v(-11.82, -0.07) * mm, "end": v(-11.67, 0.42) * mm});
            skLineSegment(sketch, "E88", {"start": v(-11.67, 0.42) * mm, "end": v(-11.67, 0.8) * mm});
            skLineSegment(sketch, "E89", {"start": v(-11.67, 0.8) * mm, "end": v(-11.86, 1.4) * mm});
            skLineSegment(sketch, "E90", {"start": v(-11.86, 1.4) * mm, "end": v(-12.48, 2.05) * mm});
            skLineSegment(sketch, "E91", {"start": v(-12.48, 2.05) * mm, "end": v(-13.51, 2.5) * mm});
            skLineSegment(sketch, "E92", {"start": v(-13.51, 2.5) * mm, "end": v(-14.4, 2.5) * mm});
            skLineSegment(sketch, "E93", {"start": v(-14.4, 2.5) * mm, "end": v(-15.64, 2.22) * mm});
            skLineSegment(sketch, "E94", {"start": v(-15.64, 2.22) * mm, "end": v(-16.35, 1.92) * mm});
            skLineSegment(sketch, "E95", {"start": v(-16.35, 1.92) * mm, "end": v(-16.9, 1.63) * mm});
            skLineSegment(sketch, "E96", {"start": v(-16.9, 1.63) * mm, "end": v(-17.31, 1.33) * mm});
            skLineSegment(sketch, "E97", {"start": v(-16.74, -0.18) * mm, "end": v(-16.58, -0.39) * mm});
            skLineSegment(sketch, "E98", {"start": v(-16.58, -0.39) * mm, "end": v(-16.22, -0.75) * mm});
            skLineSegment(sketch, "E99", {"start": v(-16.22, -0.75) * mm, "end": v(-15.95, -1.03) * mm});
            skLineSegment(sketch, "E100", {"start": v(-15.95, -1.03) * mm, "end": v(-15.64, -1.24) * mm});
            skLineSegment(sketch, "E101", {"start": v(-15.64, -1.24) * mm, "end": v(-16.27, -1.15) * mm});
            skLineSegment(sketch, "E102", {"start": v(-16.27, -1.15) * mm, "end": v(-16.74, -0.99) * mm});
            skLineSegment(sketch, "E103", {"start": v(-16.74, -0.99) * mm, "end": v(-17.08, -0.85) * mm});
            skLineSegment(sketch, "E104", {"start": v(-17.08, -0.85) * mm, "end": v(-17.3, -0.68) * mm});
            skPoint(sketch, "E105.start.orphan", {"position": v(-19.08, -1.77) * mm});
            skLineSegment(sketch, "E106.MirrorCS", {"start": v(-12.11, -3.04) * mm, "end": v(-11.82, -3.47) * mm});
            skLineSegment(sketch, "E107.MirrorCS", {"start": v(-16.35, -5.46) * mm, "end": v(-16.9, -5.17) * mm});
            skLineSegment(sketch, "E108.MirrorCS", {"start": v(-12.43, -2.84) * mm, "end": v(-12.11, -3.04) * mm});
            skLineSegment(sketch, "E109.MirrorCS", {"start": v(-13.51, -6.05) * mm, "end": v(-14.4, -6.05) * mm});
            skLineSegment(sketch, "E110.MirrorCS", {"start": v(-15.64, -2.3) * mm, "end": v(-16.27, -2.4) * mm});
            skLineSegment(sketch, "E111.MirrorCS", {"start": v(-15.8, -3.61) * mm, "end": v(-15.34, -3.16) * mm});
            skLineSegment(sketch, "E112.MirrorCS", {"start": v(-16.27, -2.4) * mm, "end": v(-16.74, -2.55) * mm});
            skLineSegment(sketch, "E113.MirrorCS", {"start": v(-16.74, -2.55) * mm, "end": v(-17.08, -2.7) * mm});
            skLineSegment(sketch, "E114.MirrorCS", {"start": v(-15.95, -2.51) * mm, "end": v(-15.64, -2.3) * mm});
            skLineSegment(sketch, "E115.MirrorCS", {"start": v(-11.67, -4.34) * mm, "end": v(-11.86, -4.95) * mm});
            skLineSegment(sketch, "E116.MirrorCS", {"start": v(-11.86, -4.95) * mm, "end": v(-12.48, -5.6) * mm});
            skLineSegment(sketch, "E117.MirrorCS", {"start": v(-16.9, -5.17) * mm, "end": v(-17.31, -4.88) * mm});
            skLineSegment(sketch, "E118.MirrorCS", {"start": v(-15.64, -5.76) * mm, "end": v(-16.35, -5.46) * mm});
            skLineSegment(sketch, "E119.MirrorCS", {"start": v(-16.58, -3.15) * mm, "end": v(-16.22, -2.8) * mm});
            skLineSegment(sketch, "E120.MirrorCS", {"start": v(-15.34, -3.16) * mm, "end": v(-14.94, -2.85) * mm});
            skLineSegment(sketch, "E121.MirrorCS", {"start": v(-11.82, -3.47) * mm, "end": v(-11.67, -3.96) * mm});
            skLineSegment(sketch, "E122.MirrorCS", {"start": v(-16.03, -3.91) * mm, "end": v(-15.8, -3.61) * mm});
            skLineSegment(sketch, "E123.MirrorCS", {"start": v(-16.74, -3.36) * mm, "end": v(-16.58, -3.15) * mm});
            skLineSegment(sketch, "E124.MirrorCS", {"start": v(-13.12, -2.53) * mm, "end": v(-12.43, -2.84) * mm});
            skLineSegment(sketch, "E125.MirrorCS", {"start": v(-16.74, -3.36) * mm, "end": v(-16.03, -3.91) * mm});
            skLineSegment(sketch, "E126.MirrorCS", {"start": v(-13.49, -2.46) * mm, "end": v(-13.12, -2.53) * mm});
            skLineSegment(sketch, "E127.MirrorCS", {"start": v(-14.94, -2.85) * mm, "end": v(-14.24, -2.54) * mm});
            skLineSegment(sketch, "E128.MirrorCS", {"start": v(-14.24, -2.54) * mm, "end": v(-13.49, -2.46) * mm});
            skLineSegment(sketch, "E129.MirrorCS", {"start": v(-16.22, -2.8) * mm, "end": v(-15.95, -2.51) * mm});
            skLineSegment(sketch, "E130.MirrorCS", {"start": v(-17.08, -2.7) * mm, "end": v(-17.3, -2.86) * mm});
            skLineSegment(sketch, "E131.MirrorCS", {"start": v(-11.67, -3.96) * mm, "end": v(-11.67, -4.34) * mm});
            skLineSegment(sketch, "E132.MirrorCS", {"start": v(-14.4, -6.05) * mm, "end": v(-15.64, -5.76) * mm});
            skLineSegment(sketch, "E133.MirrorCS", {"start": v(-17.3, -2.86) * mm, "end": v(-18.54, -1.77) * mm});
            skLineSegment(sketch, "E134.MirrorCS", {"start": v(-12.48, -5.6) * mm, "end": v(-13.51, -6.05) * mm});
            skArc(sketch, "E135", {"start": v(-17.31, -4.88) * mm, "mid": v(-7.2, -1.77) * mm, "end": v(-17.31, 1.33) * mm});
            skText(sketch, "E136", { "text": "E-Wing", "fontName": "NotoSans-Bold.ttf"});
            skLineSegment(sketch, "E137", {"start": v(-10.65, 5.83) * mm, "end": v(-10.65, 4.23) * mm, "construction": true});
            skLineSegment(sketch, "E138", {"start": v(-13.28, -10.1) * mm, "end": v(-13.67, -8.55) * mm, "construction": true});
            skLineSegment(sketch, "E139", {"start": v(-13.67, -8.55) * mm, "end": v(-2.63, -5.79) * mm, "construction": true});
            skPoint(sketch, "E140.0", {"position": v(-25.15, -17.53) * mm});
            skLineSegment(sketch, "E141", {"start": v(-25.15, -17.53) * mm, "end": v(-25.15, -16.53) * mm, "construction": true});
            skLineSegment(sketch, "E142", {"start": v(-25.15, -16.53) * mm, "end": v(-24.15, -16.53) * mm, "construction": true});
            const initialGuessF20  = {"E136": [-0.01937, -0.01653, 0, 1, 0.00478]};
            skSetInitialGuess(sketch, initialGuessF20);
            skSolve(sketch);
        }
        {
            var Q0;
            Q0=makeQuery(id+"F20.imprint","IMPRINT",FACE,{"disambiguationData":[TD([[makeQuery(id+"F20.imprint","IMPRINT",EDGE,{"derivedFrom":sQuery(id+"F20.wireOp",EDGE,"E136.sketch_text.stroke-0")}),-1.0]])]});
            var Q1;
            Q1=makeQuery(id+"F20.imprint","IMPRINT",FACE,{"disambiguationData":[TD([[makeQuery(id+"F20.imprint","IMPRINT",EDGE,{"derivedFrom":sQuery(id+"F20.wireOp",EDGE,"E136.sketch_text.stroke-12")}),-1.0]])]});
            var Q2;
            Q2=makeQuery(id+"F20.imprint","IMPRINT",FACE,{"disambiguationData":[TD([[makeQuery(id+"F20.imprint","IMPRINT",EDGE,{"derivedFrom":sQuery(id+"F20.wireOp",EDGE,"E136.sketch_text.stroke-16")}),-1.0]])]});
            var Q3;
            Q3=makeQuery(id+"F20.imprint","IMPRINT",FACE,{"disambiguationData":[TD([[makeQuery(id+"F20.imprint","IMPRINT",EDGE,{"derivedFrom":sQuery(id+"F20.wireOp",EDGE,"E136.sketch_text.stroke-40")}),-1.0]])]});
            var Q4;
            Q4=makeQuery(id+"F20.imprint","IMPRINT",FACE,{"disambiguationData":[TD([[makeQuery(id+"F20.imprint","IMPRINT",EDGE,{"derivedFrom":sQuery(id+"F20.wireOp",EDGE,"E136.sketch_text.stroke-45")}),-1.0]])]});
            var Q5;
            Q5=makeQuery(id+"F20.imprint","IMPRINT",FACE,{"disambiguationData":[TD([[makeQuery(id+"F20.imprint","IMPRINT",EDGE,{"derivedFrom":sQuery(id+"F20.wireOp",EDGE,"E136.sketch_text.stroke-49")}),-1.0]])]});
            var Q6;
            Q6=makeQuery(id+"F20.imprint","IMPRINT",FACE,{"disambiguationData":[TD([[makeQuery(id+"F20.imprint","IMPRINT",EDGE,{"derivedFrom":sQuery(id+"F20.wireOp",EDGE,"E136.sketch_text.stroke-66")}),-1.0]])]});
            var Q7;
            Q7=makeQuery(id+"F20.imprint","IMPRINT",FACE,{"disambiguationData":[TD([[makeQuery(id+"F20.imprint","IMPRINT",EDGE,{"derivedFrom":sQuery(id+"F20.wireOp",EDGE,"E76")}),1.0]])]});
            extrude(context, id + "F21", {"entities" : qUnion([Q0, Q1, Q2, Q3, Q4, Q5, Q6, Q7]), "operationType" : NewBodyOperationType.ADD, "depth" : .5 * mm, "offsetDistance" : 25 * mm});
        }
    });
